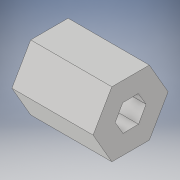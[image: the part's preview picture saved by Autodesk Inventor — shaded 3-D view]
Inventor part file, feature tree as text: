
AUTODESK INVENTOR PART (.ipt)
format: ipt  version: 2019 (Build 230136000, 136)  size: 116,224 bytes
history: native  units: in
note: dims shown in document units (in); Inventor stores cm internally (conversion verified against a paired STEP export)
features: extrude x3, sketch x2, projected_geometry x1
ambient origin geometry x8: Origin, YZ Plane, XZ Plane, XY Plane, X Axis, Y Axis, Z Axis, Center Point
bodies: Solid1 (feature_tree)
feature tree (6):
  extrude  "Extrusion1"  Depth=0.125in TaperAngle=0.0deg
  sketch  "Sketch3"  dims[d6=0.103in d8=0.5in d9=0.0in d10=0.5in d11=0.0in]
  extrude  "Extrusion3"  Depth=0.5in TaperAngle=0.0deg
  extrude  "Extrusion4"  Depth=0.5in TaperAngle=0.0deg
  sketch  "Sketch1"  dims[d0=0.25in d1=0.125in d2=0.0in]
  projected_geometry  "Projected Loop2"
